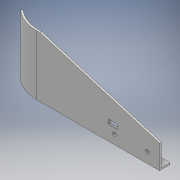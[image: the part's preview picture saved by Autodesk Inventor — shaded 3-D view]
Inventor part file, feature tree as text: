
AUTODESK INVENTOR PART (.ipt)
format: ipt  version: 2018 (Build 220112000, 112)  size: 150,016 bytes
history: native  units: mm
features: other x8, extrude x3, sketch x3, projected_geometry x2, reference x2
ambient origin geometry x8: Origin, YZ Plane, XZ Plane, XY Plane, X Axis, Y Axis, Z Axis, Center Point
bodies: Body1 (feature_tree)
feature tree (18):
  other  "endplate_ver2.ipt"
  extrude  "押し出し1"  Depth=10.0mm
  extrude  "押し出し2"  Depth=10.0mm TaperAngle=0.0deg
  extrude  "押し出し3"  Depth=10.0mm TaperAngle=0.0deg
  other  "ソリッド2::endplate_ver2.ipt"
  other  "TaggingFeature1"
  sketch  "スケッチ1"
  projected_geometry  "投影ループ1"
  projected_geometry  "投影ループ2"
  sketch  "スケッチ2"
  reference  "参照1"
  reference  "参照2"
  sketch  "スケッチ3"
  other  "ソリッド1"
  other  "<userpath>\Documents\Inventor\Aero\KS-15\Fr.wing\Fr.wing_assy.iam"
  other  "Fr.wing_assy.iam"
  other  "mainflap_side:3"
  other  "plate_ms:2"
